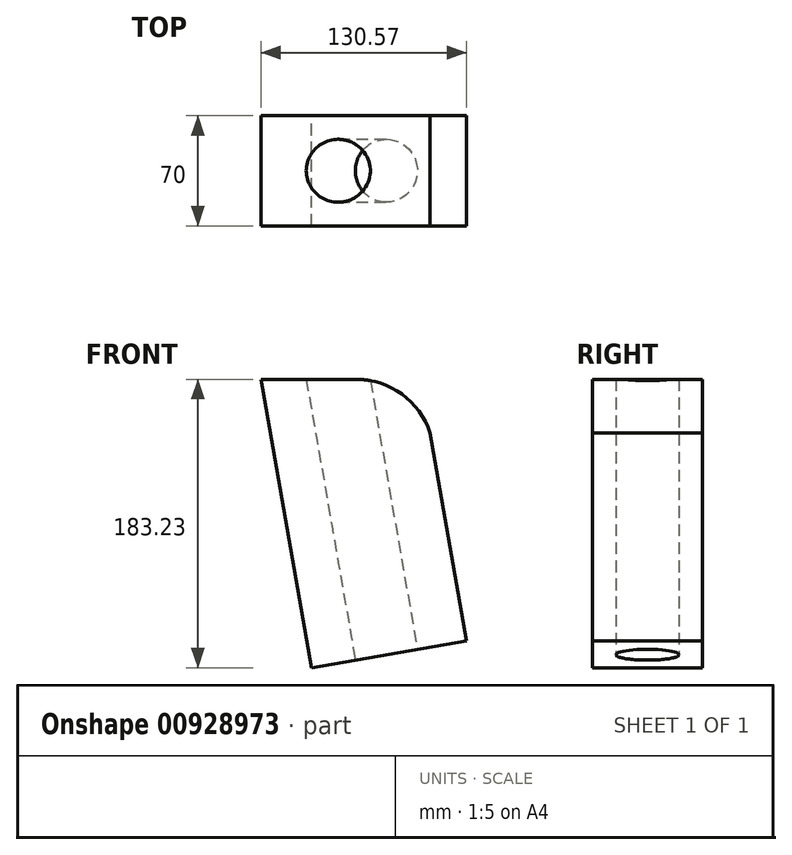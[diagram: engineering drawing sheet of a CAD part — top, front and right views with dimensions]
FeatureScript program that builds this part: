
annotation { "Feature Type Name" : "Feature", "Feature Type Description" : "" }
export const myFeature = defineFeature(function(context is Context, id is Id, definition is map)
    precondition{}
    {
        {
            var Q0;
            Q0=qCreatedBy(makeId("Front.planeOp"),FACE);
            var sketch = newSketch(context, id + "F0", { "sketchPlane" : qUnion([Q0])});
            skLineSegment(sketch, "E0", {"start": v(42.1, 58.87) * mm, "end": v(65.22, -73.19) * mm});
            skArc(sketch, "E1", {"start": v(42.1, 58.87) * mm, "mid": v(24.25, 83.42) * mm, "end": v(-4.63, 92.8) * mm});
            skLineSegment(sketch, "E2", {"start": v(-65.35, 92.8) * mm, "end": v(-33.28, -90.43) * mm});
            skLineSegment(sketch, "E3", {"start": v(-33.28, -90.43) * mm, "end": v(65.22, -73.19) * mm});
            skLineSegment(sketch, "E4.trimOffspring", {"start": v(-65.35, 92.8) * mm, "end": v(-4.63, 92.8) * mm});
            skSolve(sketch);
        }
        {
            var Q0;
            Q0=makeQuery(id+"F0.imprint","IMPRINT",FACE,{"disambiguationData":[TD([[makeQuery(id+"F0.imprint","IMPRINT",EDGE,{"derivedFrom":sQuery(id+"F0.wireOp",EDGE,"E0")}),-1.0]])]});
            extrude(context, id + "F1", {"entities" : qUnion([Q0]), "endBound" : BoundingType.SYMMETRIC, "depth" : 70 * mm, "offsetDistance" : 25 * mm});
        }
        {
            var Q0;
            Q0=makeQuery(id+"F1.opExtrude","SWEPT_FACE",FACE,{"disambiguationData":[OSD([sQuery(id+"F0.wireOp",EDGE,"E3")])]});
            var sketch = newSketch(context, id + "F2", { "sketchPlane" : qUnion([Q0])});
            skCircle(sketch, "E5", {"center": v(0, 0) * mm, "radius": 20 * mm});
            skSolve(sketch);
        }
        {
            var Q0;
            Q0=makeQuery(id+"F2.imprint","IMPRINT",FACE,{"disambiguationData":[TD([[makeQuery(id+"F2.imprint","IMPRINT",EDGE,{"derivedFrom":sQuery(id+"F2.wireOp",EDGE,"E5")}),1.0]])]});
            extrude(context, id + "F3", {"entities" : qUnion([Q0]), "operationType" : NewBodyOperationType.REMOVE, "oppositeDirection" : true, "depth" : 200 * mm, "offsetDistance" : 25 * mm});
        }
    });
